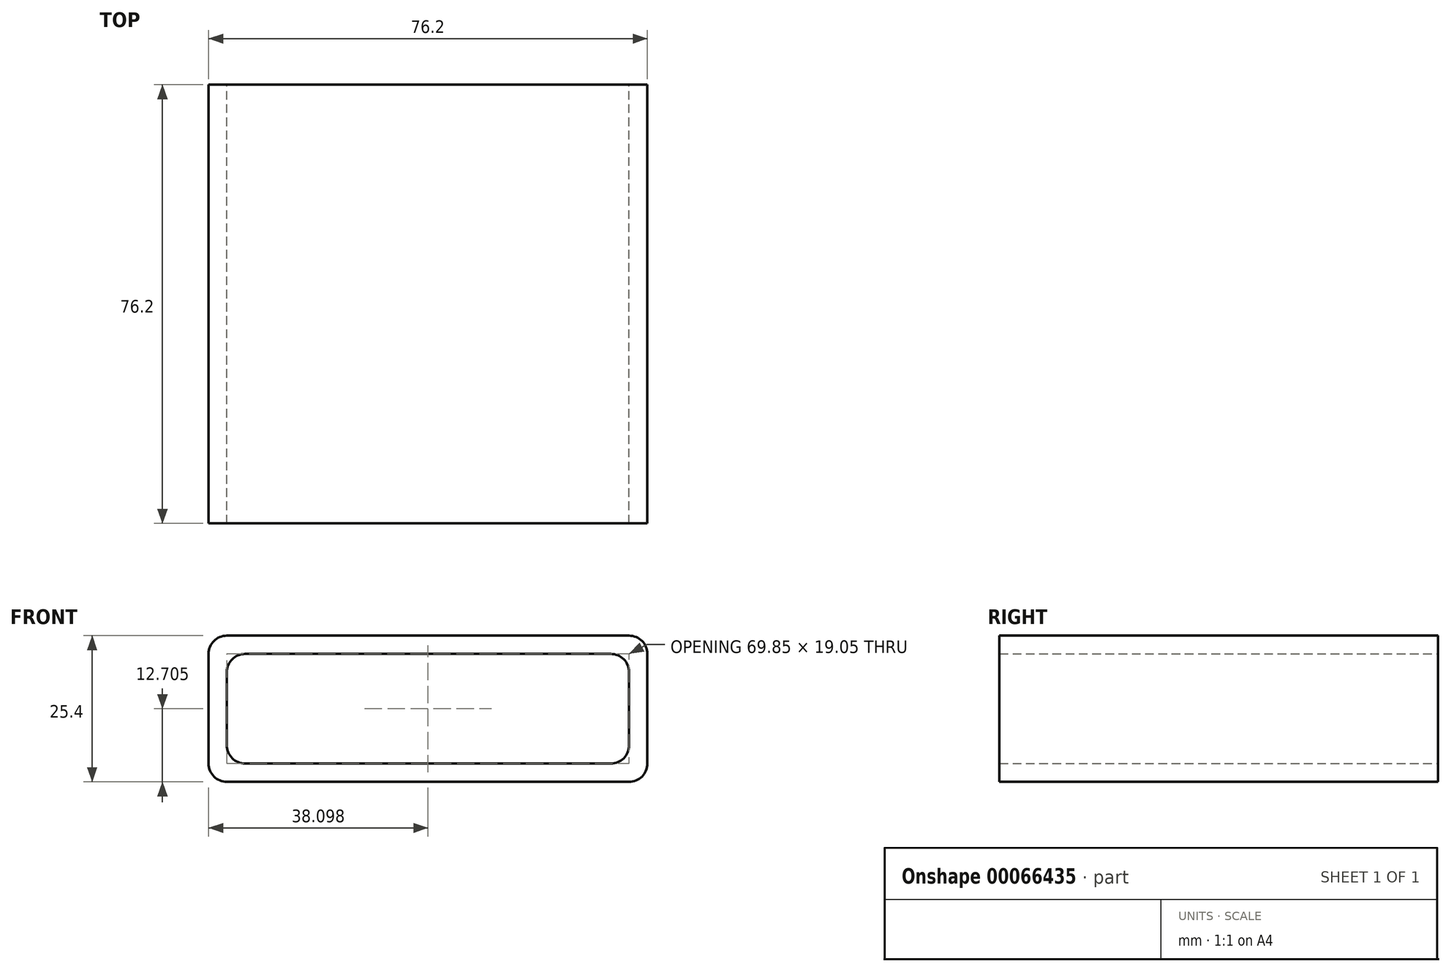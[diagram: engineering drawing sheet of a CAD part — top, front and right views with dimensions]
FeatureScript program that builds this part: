
annotation { "Feature Type Name" : "Feature", "Feature Type Description" : "" }
export const myFeature = defineFeature(function(context is Context, id is Id, definition is map)
    precondition{}
    {
        {
            var Q0;
            Q0=qCreatedBy(makeId("Front.planeOp"),FACE);
            var sketch = newSketch(context, id + "F0", { "sketchPlane" : qUnion([Q0])});
            skLineSegment(sketch, "E0.bottom", {"start": v(-18.38, 29.02) * mm, "end": v(57.82, 29.02) * mm});
            skLineSegment(sketch, "E0.top", {"start": v(-18.38, 3.62) * mm, "end": v(57.82, 3.62) * mm});
            skLineSegment(sketch, "E0.left", {"start": v(-18.38, 29.02) * mm, "end": v(-18.38, 3.62) * mm});
            skLineSegment(sketch, "E0.right", {"start": v(57.82, 29.02) * mm, "end": v(57.82, 3.62) * mm});
            skSolve(sketch);
        }
        {
            var Q0;
            Q0 = qSketchRegion(id + "F0", true);
            extrude(context, id + "F1", {"entities" : qUnion([Q0]), "depth" : 76.2 * mm});
        }
        {
            var Q0;
            Q0=makeQuery(id+"F1.opExtrude","CAP_FACE",FACE,{"disambiguationData":[OSD([sQuery(id+"F0.wireOp",EDGE,"E0.bottom"),sQuery(id+"F0.wireOp",EDGE,"E0.top"),sQuery(id+"F0.wireOp",EDGE,"E0.left"),sQuery(id+"F0.wireOp",EDGE,"E0.right")])],"isStart":false});
            var Q1;
            Q1=makeQuery(id+"F1.opExtrude","CAP_FACE",FACE,{"disambiguationData":[OSD([sQuery(id+"F0.wireOp",EDGE,"E0.bottom"),sQuery(id+"F0.wireOp",EDGE,"E0.top"),sQuery(id+"F0.wireOp",EDGE,"E0.left"),sQuery(id+"F0.wireOp",EDGE,"E0.right")])],"isStart":true});
            shell(context, id + "F2", {"entities" : qUnion([Q0, Q1]), "thickness" : 3.17 * mm});
        }
        {
            var Q0;
            Q0=makeQuery(id+"F1.opExtrude","SWEPT_EDGE",EDGE,{"disambiguationData":[OSD([sQuery(id+"F0.wireOp",EDGE,"E0.bottom"),sQuery(id+"F0.wireOp",EDGE,"E0.left")])]});
            var Q1;
            Q1=makeQuery(id+"F2.opShell","OFFSET_EDGE",EDGE,{"disambiguationData":[OSD([sQuery(id+"F0.wireOp",EDGE,"E0.bottom"),sQuery(id+"F0.wireOp",EDGE,"E0.left")])]});
            var Q2;
            Q2=makeQuery(id+"F2.opShell","OFFSET_EDGE",EDGE,{"disambiguationData":[OSD([sQuery(id+"F0.wireOp",EDGE,"E0.top"),sQuery(id+"F0.wireOp",EDGE,"E0.left")])]});
            var Q3;
            Q3=makeQuery(id+"F2.opShell","OFFSET_EDGE",EDGE,{"disambiguationData":[OSD([sQuery(id+"F0.wireOp",EDGE,"E0.top"),sQuery(id+"F0.wireOp",EDGE,"E0.right")])]});
            var Q4;
            Q4=makeQuery(id+"F2.opShell","OFFSET_EDGE",EDGE,{"disambiguationData":[OSD([sQuery(id+"F0.wireOp",EDGE,"E0.bottom"),sQuery(id+"F0.wireOp",EDGE,"E0.right")])]});
            var Q5;
            Q5=makeQuery(id+"F1.opExtrude","SWEPT_EDGE",EDGE,{"disambiguationData":[OSD([sQuery(id+"F0.wireOp",EDGE,"E0.top"),sQuery(id+"F0.wireOp",EDGE,"E0.left")])]});
            var Q6;
            Q6=makeQuery(id+"F1.opExtrude","SWEPT_EDGE",EDGE,{"disambiguationData":[OSD([sQuery(id+"F0.wireOp",EDGE,"E0.bottom"),sQuery(id+"F0.wireOp",EDGE,"E0.right")])]});
            var Q7;
            Q7=makeQuery(id+"F1.opExtrude","SWEPT_EDGE",EDGE,{"disambiguationData":[OSD([sQuery(id+"F0.wireOp",EDGE,"E0.top"),sQuery(id+"F0.wireOp",EDGE,"E0.right")])]});
            fillet(context, id + "F3", {"entities" : qUnion([Q0, Q1, Q2, Q3, Q4, Q5, Q6, Q7]), "radius" : 3.17 * mm, "tangentPropagation" : true, "allowEdgeOverflow" : false});
        }
    });
